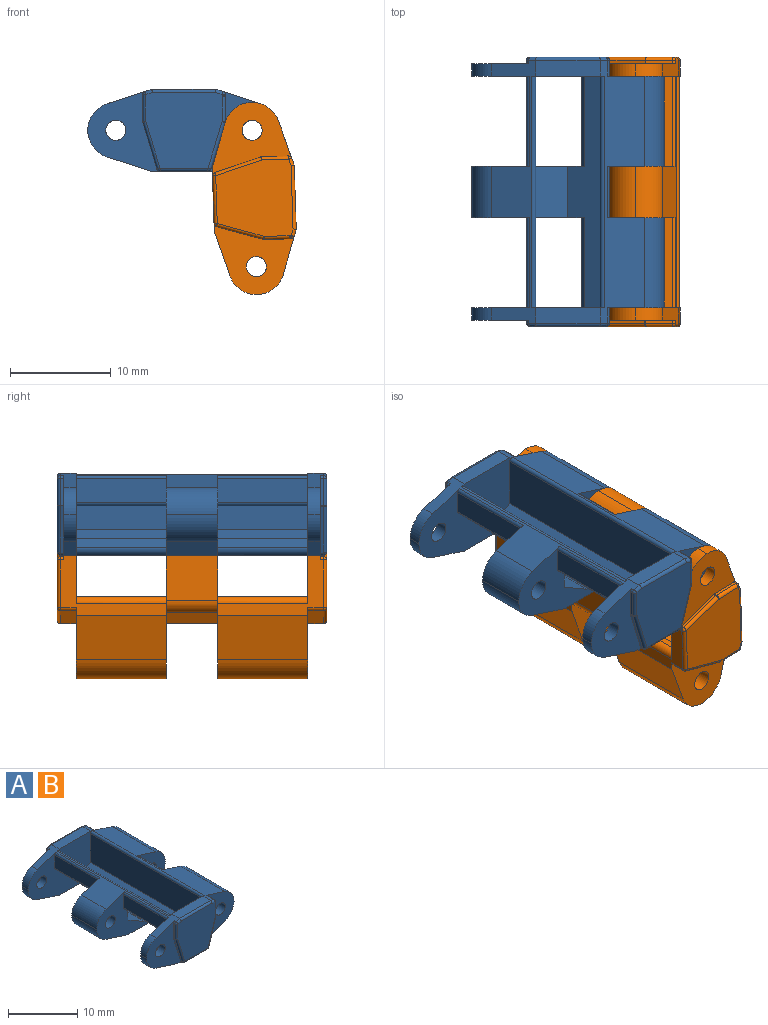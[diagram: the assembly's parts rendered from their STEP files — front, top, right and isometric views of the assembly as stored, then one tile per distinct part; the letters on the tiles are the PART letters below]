
ASSEMBLY  parts=2 mates=1
PART A: 107 faces, bbox 19.1x26.7x8.1 mm
  f0: plane 7.89x7.15mm, normal (0,-1,0), area 30.3mm2, adj f13,f14,f17,f24,f26,f38,f59,f60
  f1: plane 7.89x7.15mm, normal (0,1,0), area 30.3mm2, adj f4,f14,f16,f30,f33,f40,f56,f57
  f2: cylinder r=1.27mm len=5.08mm, axis (0,1,0), area 8.2mm2, adj f3,f5,f8,f9,f10,f11
  f3: plane 7.89x7.7mm, normal (0,1,0), area 30.4mm2, adj f2,f11,f17,f18,f23,f28,f29,f36
  f4: plane 10.48x6.36mm, normal (0,0,-1), area 19.5mm2, adj f1,f7,f8,f16,f19,f51,f54,f67
  f5: plane 5.08x4.85mm, normal (0,0,-1), area 24.6mm2, adj f2,f9,f10,f15
  f6: plane 22.91x5.08mm, normal (-1,0,0), area 116.3mm2, adj f7,f20,f21,f73
  f7: plane 13.12x8.12mm, normal (0,-1,0), area 79.2mm2, adj f4,f6,f12,f14,f16,f18,f21,f30
  f8: plane 7.89x7.7mm, normal (0,-1,0), area 30.4mm2, adj f2,f4,f11,f18,f19,f31,f32,f37
  f9: plane 11.35x7.9mm, normal (0,-1,0), area 38.2mm2, adj f2,f5,f12,f14,f15,f21,f22,f25
  f10: plane 11.35x7.9mm, normal (0,1,0), area 38.2mm2, adj f2,f5,f12,f14,f15,f21,f22,f25
  f11: plane 5.08x4.01mm, normal (0.96,0,-0.29), area 21.3mm2, adj f2,f3,f8,f45
  f12: plane 22.91x5.08mm, normal (1,0,0), area 69.6mm2, adj f7,f9,f10,f20,f22,f74,f103,f104
  f13: plane 4.41x1.41mm, normal (-0.31,0,-0.95), area 5.8mm2, adj f0,f17,f20,f24
  f14: plane 26.04x4.41mm, normal (-0.31,0,0.95), area 38.2mm2, adj f0,f1,f7,f9,f10,f20,f26,f27
  f15: plane 5.08x4.41mm, normal (-0.31,0,-0.95), area 23.5mm2, adj f5,f9,f10,f25
  f16: plane 4.41x1.41mm, normal (-0.31,0,-0.95), area 5.8mm2, adj f1,f4,f7,f30
  f17: plane 10.48x6.36mm, normal (0,0,-1), area 19.5mm2, adj f0,f3,f13,f20,f23,f50,f55,f65
  f18: plane 26.04x4.41mm, normal (0.31,0,0.95), area 78.7mm2, adj f3,f7,f8,f20,f29,f32,f34,f35
  f19: plane 8.92x4.41mm, normal (0.31,0,-0.95), area 41.3mm2, adj f4,f8,f31,f51
  f20: plane 13.12x8.12mm, normal (0,1,0), area 79.2mm2, adj f6,f12,f13,f14,f17,f18,f21,f24
  f21: plane 22.91x3.18mm, normal (-0.5,0,0.87), area 51.4mm2, adj f6,f7,f9,f10,f20,f22,f52,f53
  f22: plane 5.08x3.18mm, normal (0.5,0,0.87), area 18.7mm2, adj f9,f10,f12,f21
  f23: plane 8.92x4.41mm, normal (0.31,0,-0.95), area 41.3mm2, adj f3,f17,f28,f50
  f24: cylinder r=2.78mm len=2.65mm, axis (0,1,0), area 4.4mm2, adj f0,f13,f20,f26
  f25: cylinder r=2.78mm len=5.08mm, axis (0,1,0), area 17.8mm2, adj f9,f10,f15,f27
  f26: cylinder r=2.78mm len=2.65mm, axis (0,-1,0), area 4.4mm2, adj f0,f14,f20,f24
  f27: cylinder r=2.78mm len=5.08mm, axis (0,-1,0), area 17.8mm2, adj f9,f10,f14,f25
  f28: cylinder r=2.78mm len=8.92mm, axis (0,1,0), area 31.2mm2, adj f3,f23,f29,f50
  f29: cylinder r=2.78mm len=8.92mm, axis (0,-1,0), area 31.2mm2, adj f3,f18,f28,f50
  f30: cylinder r=2.78mm len=2.65mm, axis (0,1,0), area 4.4mm2, adj f1,f7,f16,f33
  f31: cylinder r=2.78mm len=8.92mm, axis (0,1,0), area 31.2mm2, adj f8,f19,f32,f51
  f32: cylinder r=2.78mm len=8.92mm, axis (0,-1,0), area 31.2mm2, adj f8,f18,f31,f51
  f33: cylinder r=2.78mm len=2.65mm, axis (0,-1,0), area 4.4mm2, adj f1,f7,f14,f30
  f34: plane 6.36x1.56mm, normal (0,0,1), area 9.9mm2, adj f7,f14,f18,f83
  f35: plane 6.36x1.56mm, normal (0,0,1), area 9.9mm2, adj f14,f18,f20,f96
  f36: cylinder r=1mm len=8.92mm, axis (0,-1,0), area 56mm2, adj f3,f50
  f37: cylinder r=1mm len=8.92mm, axis (0,-1,0), area 56mm2, adj f8,f51
  f38: cylinder r=1mm len=2mm, axis (0,-1,0), area 7.8mm2, adj f0,f20
  f39: cylinder r=1mm len=5.08mm, axis (0,-1,0), area 31.9mm2, adj f9,f10
  f40: cylinder r=1mm len=2mm, axis (0,-1,0), area 7.8mm2, adj f1,f7
  f41: plane 4.68x1.56mm, normal (0.96,0,-0.29), area 7.6mm2, adj f42,f50,f62,f69,f87
  f42: plane 2.69x1.56mm, normal (1,0,0), area 4.2mm2, adj f41,f50,f62,f72,f90
  f43: plane 4.68x1.56mm, normal (0.96,0,-0.29), area 7.6mm2, adj f44,f51,f68,f75
  f44: plane 2.69x1.56mm, normal (1,0,0), area 4.2mm2, adj f43,f51,f70,f77
  f45: plane 5.08x2.69mm, normal (1,0,0), area 13.6mm2, adj f3,f8,f11,f71
  f46: plane 8.92x2.34mm, normal (-1,0,0), area 20.9mm2, adj f7,f10,f102,f106
  f47: plane 8.92x2.34mm, normal (-1,0,0), area 20.9mm2, adj f9,f20,f101,f105
  f48: plane 8.92x0.29mm, normal (0,0,-1), area 2.5mm2, adj f9,f20,f103,f105
  f49: plane 8.92x0.29mm, normal (0,0,-1), area 2.5mm2, adj f7,f10,f104,f106
  f50: plane 7.89x7.15mm, normal (0,-1,0), area 30.3mm2, adj f17,f18,f23,f28,f29,f36,f41,f42
  f51: plane 7.89x7.15mm, normal (0,1,0), area 30.3mm2, adj f4,f18,f19,f31,f32,f37,f43,f44
  f52: plane 8.92x0.87mm, normal (-0.96,0,0.29), area 8.1mm2, adj f9,f20,f21,f55
  f53: plane 8.92x0.87mm, normal (-0.96,0,0.29), area 8.1mm2, adj f7,f10,f21,f54
  f54: cylinder r=0.64mm len=8.92mm, axis (0,-1,0), area 10.6mm2, adj f4,f7,f8,f10,f53
  f55: cylinder r=0.64mm len=8.92mm, axis (0,-1,0), area 10.6mm2, adj f3,f9,f17,f20,f52
  f56: plane 4.68x1.43mm, normal (-0.96,0,-0.29), area 1.6mm2, adj f1,f57,f67,f82
  f57: plane 2.69x0.32mm, normal (-1,0,0), area 0.9mm2, adj f1,f56,f66,f84
  f58: plane 7.57x7.48mm, normal (0,1,0), area 50mm2, adj f75,f77,f78,f81,f82,f83,f84,f85
  f59: plane 2.69x0.32mm, normal (-1,0,0), area 0.9mm2, adj f0,f60,f64,f99
  f60: cylinder r=2.78mm len=0.32mm, axis (0,1,0), area 0mm2, adj f0,f59,f61,f97
  f61: plane 4.6x1.4mm, normal (-0.96,0,-0.29), area 1.5mm2, adj f0,f60,f65,f95
  f62: cylinder r=2.78mm len=0.32mm, axis (0,1,0), area 0mm2, adj f41,f42,f88
  f63: plane 7.57x7.48mm, normal (0,-1,0), area 50mm2, adj f87,f88,f90,f91,f94,f95,f96,f97
  f64: cylinder r=0.32mm len=0.32mm, axis (0,-1,0), area 0.1mm2, adj f0,f14,f59,f100
  f65: cylinder r=0.32mm len=0.32mm, axis (0,1,0), area 0.1mm2, adj f0,f17,f61,f93
  f66: cylinder r=0.32mm len=0.32mm, axis (0,-1,0), area 0.1mm2, adj f1,f14,f57,f86
  f67: cylinder r=0.32mm len=0.32mm, axis (0,-1,0), area 0.1mm2, adj f1,f4,f56,f80
  f68: cylinder r=0.32mm len=1.56mm, axis (0,1,0), area 0.6mm2, adj f4,f43,f51,f76
  f69: cylinder r=0.32mm len=1.56mm, axis (0,1,0), area 0.6mm2, adj f17,f41,f50,f89
  f70: cylinder r=0.32mm len=1.56mm, axis (0,1,0), area 0.6mm2, adj f18,f44,f51,f79
  f71: cylinder r=0.32mm len=5.08mm, axis (0,1,0), area 2mm2, adj f3,f8,f18,f45
  f72: cylinder r=0.32mm len=1.56mm, axis (0,1,0), area 0.6mm2, adj f18,f42,f50,f92
  f73: cylinder r=0.32mm len=22.91mm, axis (0,-1,0), area 13.7mm2, adj f6,f7,f18,f20
  f74: cylinder r=0.32mm len=22.91mm, axis (0,-1,0), area 13.7mm2, adj f7,f12,f14,f20
  f75: cylinder r=0.32mm len=4.77mm, axis (0.29,0,0.96), area 2.4mm2, adj f43,f58,f76,f77
  f76: sphere r=0.32mm, area 0.1mm2, adj f68,f75,f78
  f77: cylinder r=0.32mm len=2.69mm, axis (0,0,-1), area 1.3mm2, adj f44,f58,f75,f79
  f78: cylinder r=0.32mm len=4.75mm, axis (1,0,0), area 2.4mm2, adj f4,f58,f76,f80
  f79: sphere r=0.32mm, area 0.1mm2, adj f70,f77,f81
  f80: sphere r=0.32mm, area 0.1mm2, adj f67,f78,f82
  f81: cylinder r=0.32mm len=0.8mm, axis (-0.95,0,0.31), area 0.4mm2, adj f18,f58,f79,f83
  f82: cylinder r=0.32mm len=4.77mm, axis (0.29,0,-0.96), area 2.4mm2, adj f56,f58,f80,f84
  f83: cylinder r=0.32mm len=6.36mm, axis (1,0,0), area 3.1mm2, adj f34,f58,f81,f85
  f84: cylinder r=0.32mm len=2.69mm, axis (0,0,-1), area 1.3mm2, adj f57,f58,f82,f86
  f85: cylinder r=0.32mm len=0.8mm, axis (0.95,0,0.31), area 0.4mm2, adj f14,f58,f83,f86
  f86: sphere r=0.32mm, area 0.1mm2, adj f66,f84,f85
  f87: cylinder r=0.32mm len=4.7mm, axis (-0.29,0,-0.96), area 2.4mm2, adj f41,f63,f88,f89
  f88: torus R=3.1mm, axis (0,-1,0), area 0mm2, adj f62,f63,f87,f90
  f89: sphere r=0.32mm, area 0.1mm2, adj f69,f87,f91
  f90: cylinder r=0.32mm len=2.69mm, axis (0,0,-1), area 1.3mm2, adj f42,f63,f88,f92
  f91: cylinder r=0.32mm len=4.75mm, axis (-1,0,0), area 2.4mm2, adj f17,f63,f89,f93
  f92: sphere r=0.32mm, area 0.2mm2, adj f72,f90,f94
  f93: sphere r=0.32mm, area 0.1mm2, adj f65,f91,f95
  f94: cylinder r=0.32mm len=0.8mm, axis (-0.95,0,0.31), area 0.4mm2, adj f18,f63,f92,f96
  f95: cylinder r=0.32mm len=4.7mm, axis (-0.29,0,0.96), area 2.4mm2, adj f61,f63,f93,f97
  f96: cylinder r=0.32mm len=6.36mm, axis (-1,0,0), area 3.1mm2, adj f35,f63,f94,f98
  f97: torus R=3.1mm, axis (0,-1,0), area 0mm2, adj f60,f63,f95,f99
  f98: cylinder r=0.32mm len=0.8mm, axis (-0.95,0,-0.31), area 0.4mm2, adj f14,f63,f96,f100
  f99: cylinder r=0.32mm len=2.69mm, axis (0,0,1), area 1.3mm2, adj f59,f63,f97,f100
  f100: sphere r=0.32mm, area 0.1mm2, adj f64,f98,f99
  f101: cylinder r=0.36mm len=8.92mm, axis (0,1,0), area 4mm2, adj f9,f14,f20,f47
  f102: cylinder r=0.36mm len=8.92mm, axis (0,1,0), area 4mm2, adj f7,f10,f14,f46
  f103: cylinder r=0.32mm len=8.92mm, axis (0,-1,0), area 4.4mm2, adj f9,f12,f20,f48
  f104: cylinder r=0.32mm len=8.92mm, axis (0,1,0), area 4.4mm2, adj f7,f10,f12,f49
  f105: cylinder r=0.32mm len=8.92mm, axis (0,1,0), area 4.4mm2, adj f9,f20,f47,f48
  f106: cylinder r=0.32mm len=8.92mm, axis (0,1,0), area 4.4mm2, adj f7,f10,f46,f49
PART B: same geometry as A
PLACE A t=(-10.58,-6,3.85)mm fixed
PLACE B rot(axis=(0,1,0),88.2deg) t=(1.55,-6,10.56)mm
MATE planar A.f0 <-> B.f0  axis (0,-1,0) through (-7.1,-6,7.63)mm
